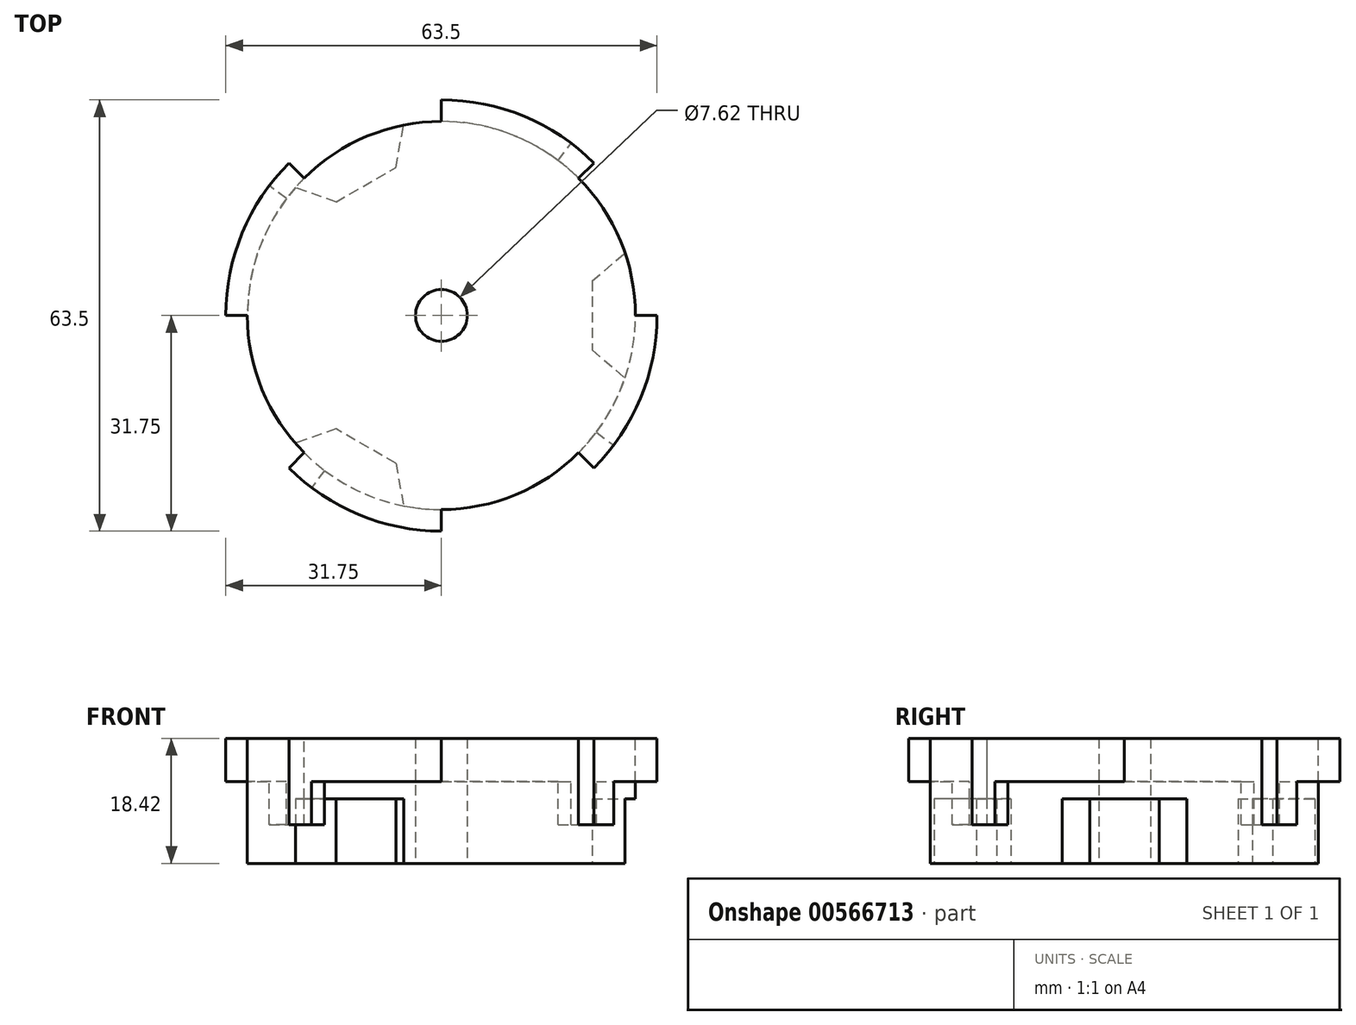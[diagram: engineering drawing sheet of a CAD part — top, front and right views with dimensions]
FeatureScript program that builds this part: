
annotation { "Feature Type Name" : "Feature", "Feature Type Description" : "" }
export const myFeature = defineFeature(function(context is Context, id is Id, definition is map)
    precondition{}
    {
        {
            var Q0;
            Q0=qCreatedBy(makeId("Top.planeOp"),FACE);
            var sketch = newSketch(context, id + "F0", { "sketchPlane" : qUnion([Q0])});
            skCircle(sketch, "E0", {"center": v(0, 0) * mm, "radius": 28.58 * mm});
            skLineSegment(sketch, "E1", {"start": v(22.23, 0) * mm, "end": v(22.23, 5.08) * mm});
            skLineSegment(sketch, "E2", {"start": v(22.23, 5.08) * mm, "end": v(27.05, 9.2) * mm});
            skLineSegment(sketch, "E3", {"start": v(22.23, 0) * mm, "end": v(22.23, -5.08) * mm});
            skLineSegment(sketch, "E4", {"start": v(22.23, -5.08) * mm, "end": v(27.05, -9.2) * mm});
            skLineSegment(sketch, "E5.1.0", {"start": v(-11.11, 19.25) * mm, "end": v(-15.51, 16.7) * mm});
            skLineSegment(sketch, "E5.1.1", {"start": v(-11.11, 19.25) * mm, "end": v(-6.71, 21.79) * mm});
            skLineSegment(sketch, "E5.1.2", {"start": v(-6.71, 21.79) * mm, "end": v(-5.55, 28.03) * mm});
            skLineSegment(sketch, "E5.1.3", {"start": v(-15.51, 16.7) * mm, "end": v(-21.5, 18.82) * mm});
            skLineSegment(sketch, "E5.2.0", {"start": v(-11.11, -19.25) * mm, "end": v(-6.71, -21.79) * mm});
            skLineSegment(sketch, "E5.2.1", {"start": v(-11.11, -19.25) * mm, "end": v(-15.51, -16.7) * mm});
            skLineSegment(sketch, "E5.2.2", {"start": v(-15.51, -16.7) * mm, "end": v(-21.5, -18.82) * mm});
            skLineSegment(sketch, "E5.2.3", {"start": v(-6.71, -21.79) * mm, "end": v(-5.55, -28.03) * mm});
            skCircle(sketch, "E6", {"center": v(0, 0) * mm, "radius": 3.81 * mm});
            skSolve(sketch);
        }
        {
            var Q0;
            Q0=makeQuery(id+"F0.imprint","IMPRINT",FACE,{"disambiguationData":[TD([[makeQuery(id+"F0.imprint","IMPRINT",EDGE,{"derivedFrom":sQuery(id+"F0.wireOp",EDGE,"E1")}),1.0]])]});
            extrude(context, id + "F1", {"entities" : qUnion([Q0]), "depth" : 9.52 * mm, "offsetDistance" : 25.4 * mm});
        }
        {
            var Q0;
            Q0=makeQuery(id+"F1.opExtrude","CAP_FACE",FACE,{"disambiguationData":[OSD([sQuery(id+"F0.wireOp",EDGE,"E0"),sQuery(id+"F0.wireOp",EDGE,"E1"),sQuery(id+"F0.wireOp",EDGE,"E2"),sQuery(id+"F0.wireOp",EDGE,"E3"),sQuery(id+"F0.wireOp",EDGE,"E4"),sQuery(id+"F0.wireOp",EDGE,"E5.1.0"),sQuery(id+"F0.wireOp",EDGE,"E5.1.1"),sQuery(id+"F0.wireOp",EDGE,"E5.1.2"),sQuery(id+"F0.wireOp",EDGE,"E5.1.3"),sQuery(id+"F0.wireOp",EDGE,"E5.2.0"),sQuery(id+"F0.wireOp",EDGE,"E5.2.1"),sQuery(id+"F0.wireOp",EDGE,"E5.2.2"),sQuery(id+"F0.wireOp",EDGE,"E5.2.3"),sQuery(id+"F0.wireOp",EDGE,"E6")])],"isStart":false});
            var sketch = newSketch(context, id + "F2", { "sketchPlane" : qUnion([Q0])});
            skCircle(sketch, "E7", {"center": v(0, 0) * mm, "radius": 28.58 * mm});
            skLineSegment(sketch, "E8", {"start": v(-21.5, 18.82) * mm, "end": v(-18.24, 17.67) * mm});
            skLineSegment(sketch, "E9", {"start": v(-5.55, 28.03) * mm, "end": v(-6.18, 24.64) * mm});
            skLineSegment(sketch, "E10", {"start": v(27.05, 9.2) * mm, "end": v(24.43, 6.96) * mm});
            skLineSegment(sketch, "E11", {"start": v(27.05, -9.2) * mm, "end": v(24.43, -6.96) * mm});
            skLineSegment(sketch, "E12", {"start": v(-21.5, -18.82) * mm, "end": v(-18.24, -17.67) * mm});
            skLineSegment(sketch, "E13", {"start": v(-5.55, -28.03) * mm, "end": v(-6.18, -24.64) * mm});
            skCircle(sketch, "E14", {"center": v(0, 0) * mm, "radius": 3.81 * mm});
            skSolve(sketch);
        }
        {
            var Q0;
            Q0 = qSketchRegion(id + "F2", true);
            var Q1;
            Q1 = qSketchRegion(id + "F4", true);
            extrude(context, id + "F3", {"entities" : qUnion([Q0, Q1]), "operationType" : NewBodyOperationType.ADD, "depth" : 8.9 * mm, "offsetDistance" : 25.4 * mm});
        }
        {
            var Q0;
            Q0=qCreatedBy(makeId("Right.planeOp"),FACE);
            var sketch = newSketch(context, id + "F4", { "sketchPlane" : qUnion([Q0])});
            skLineSegment(sketch, "E15", {"start": v(0, 0) * mm, "end": v(-28.58, 0) * mm});
            skLineSegment(sketch, "E16", {"start": v(-28.58, 0) * mm, "end": v(-28.58, 18.41) * mm});
            skLineSegment(sketch, "E17", {"start": v(-28.58, 18.41) * mm, "end": v(-31.75, 18.41) * mm});
            skLineSegment(sketch, "E18", {"start": v(-31.75, 18.41) * mm, "end": v(-31.75, 12.06) * mm});
            skLineSegment(sketch, "E19", {"start": v(-31.75, 12.06) * mm, "end": v(-28.58, 12.06) * mm});
            skLineSegment(sketch, "E20", {"start": v(0, 0) * mm, "end": v(0, 23.45) * mm});
            skSolve(sketch);
        }
        {
            var Q0;
            Q0 = qSketchRegion(id + "F4", true);
            var Q1;
            Q1=sQuery(id+"F4.wireOp",EDGE,"E20");
            revolve(context, id + "F5", {"operationType" : NewBodyOperationType.ADD, "entities" : qUnion([Q0]), "axis" : qUnion([Q1]), "revolveType" : RevolveType.FULL});
        }
        {
            var Q0;
            Q0=makeQuery(id+"F5.boolean.opBoolean","MERGE",FACE,{"derivedFrom":[makeQuery(id+"F3.opExtrude","CAP_FACE",FACE,{"disambiguationData":[OSD([sQuery(id+"F2.wireOp",EDGE,"E7"),sQuery(id+"F2.wireOp",EDGE,"E14")])],"isStart":false}),makeQuery(id+"F5.opRevolve","SWEPT_FACE",FACE,{"disambiguationData":[OSD([sQuery(id+"F4.wireOp",EDGE,"E17")])]})]});
            var sketch = newSketch(context, id + "F6", { "sketchPlane" : qUnion([Q0])});
            skArc(sketch, "E21", {"start": v(28.58, 0) * mm, "mid": v(26.4, 10.94) * mm, "end": v(20.2, 20.2) * mm});
            skArc(sketch, "E22", {"start": v(31.75, 0) * mm, "mid": v(29.33, 12.15) * mm, "end": v(22.45, 22.45) * mm});
            skLineSegment(sketch, "E23", {"start": v(28.58, 0) * mm, "end": v(31.75, 0) * mm});
            skLineSegment(sketch, "E24", {"start": v(0, 28.58) * mm, "end": v(0, 31.75) * mm});
            skLineSegment(sketch, "E25", {"start": v(0, -28.58) * mm, "end": v(0, -31.75) * mm});
            skLineSegment(sketch, "E26", {"start": v(-28.58, 0) * mm, "end": v(-31.75, 0) * mm});
            skLineSegment(sketch, "E27", {"start": v(20.2, -20.2) * mm, "end": v(22.45, -22.45) * mm});
            skLineSegment(sketch, "E28", {"start": v(20.2, 20.2) * mm, "end": v(22.45, 22.45) * mm});
            skLineSegment(sketch, "E29", {"start": v(-20.2, -20.2) * mm, "end": v(-22.45, -22.45) * mm});
            skLineSegment(sketch, "E30", {"start": v(-20.2, 20.2) * mm, "end": v(-22.45, 22.45) * mm});
            skArc(sketch, "E31.trimOffspring", {"start": v(0, -28.58) * mm, "mid": v(10.94, -26.4) * mm, "end": v(20.2, -20.2) * mm});
            skArc(sketch, "E32.trimOffspring", {"start": v(0, -31.75) * mm, "mid": v(12.15, -29.33) * mm, "end": v(22.45, -22.45) * mm});
            skArc(sketch, "E33.trimOffspring", {"start": v(-28.58, 0) * mm, "mid": v(-26.4, -10.94) * mm, "end": v(-20.2, -20.2) * mm});
            skArc(sketch, "E34.trimOffspring", {"start": v(-31.75, 0) * mm, "mid": v(-29.33, -12.15) * mm, "end": v(-22.45, -22.45) * mm});
            skArc(sketch, "E35.trimOffspring", {"start": v(0, 28.58) * mm, "mid": v(-10.94, 26.4) * mm, "end": v(-20.2, 20.2) * mm});
            skArc(sketch, "E36.trimOffspring", {"start": v(0, 31.75) * mm, "mid": v(-12.15, 29.33) * mm, "end": v(-22.45, 22.45) * mm});
            skSolve(sketch);
        }
        {
            var Q0;
            Q0 = qSketchRegion(id + "F6", true);
            extrude(context, id + "F7", {"entities" : qUnion([Q0]), "operationType" : NewBodyOperationType.REMOVE, "oppositeDirection" : true, "depth" : 6.35 * mm, "offsetDistance" : 25.4 * mm});
        }
        {
            var Q0;
            Q0=makeQuery(id+"F7.boolean.opBoolean","SPLIT",FACE,{"disambiguationData":[TD([makeQuery(id+"F7.opExtrude","SWEPT_FACE",FACE,{"disambiguationData":[OSD([sQuery(id+"F6.wireOp",EDGE,"E23")])]})])],"derivedFrom":makeQuery(id+"F5.opRevolve","SWEPT_FACE",FACE,{"disambiguationData":[OSD([sQuery(id+"F4.wireOp",EDGE,"E19")])]})});
            var sketch = newSketch(context, id + "F8", { "sketchPlane" : qUnion([Q0])});
            skCircle(sketch, "E37", {"center": v(0, 0) * mm, "radius": 31.75 * mm});
            skCircle(sketch, "E38", {"center": v(0, 0) * mm, "radius": 28.58 * mm});
            skLineSegment(sketch, "E39", {"start": v(20.2, 20.2) * mm, "end": v(22.45, 22.45) * mm});
            skLineSegment(sketch, "E40", {"start": v(0, 0) * mm, "end": v(25.36, 19.1) * mm});
            skLineSegment(sketch, "E41.1.0", {"start": v(20.2, -20.2) * mm, "end": v(22.45, -22.45) * mm});
            skLineSegment(sketch, "E41.1.2", {"start": v(0, 0) * mm, "end": v(19.1, -25.36) * mm});
            skLineSegment(sketch, "E41.2.0", {"start": v(-20.2, -20.2) * mm, "end": v(-22.45, -22.45) * mm});
            skLineSegment(sketch, "E41.2.2", {"start": v(0, 0) * mm, "end": v(-25.36, -19.1) * mm});
            skLineSegment(sketch, "E41.3.0", {"start": v(-20.2, 20.2) * mm, "end": v(-22.45, 22.45) * mm});
            skLineSegment(sketch, "E41.3.2", {"start": v(0, 0) * mm, "end": v(-19.1, 25.36) * mm});
            skLineSegment(sketch, "E41.anchor1", {"start": v(0, 0) * mm, "end": v(20.2, 20.2) * mm, "construction": true});
            skLineSegment(sketch, "E41.anchor2", {"start": v(0, 0) * mm, "end": v(-20.2, 20.2) * mm, "construction": true});
            skSolve(sketch);
        }
        {
            var Q0;
            {var subQ0=sQuery(id+"F8.wireOp",EDGE,"E39");Q0=makeQuery(id+"F8.imprint","IMPRINT",FACE,{"disambiguationData":[TD([[makeQuery(id+"F8.imprint","IMPRINT",EDGE,{"derivedFrom":subQ0}),-1.0]])]});}
            var Q1;
            {var subQ0=sQuery(id+"F8.wireOp",EDGE,"E41.1.0");Q1=makeQuery(id+"F8.imprint","IMPRINT",FACE,{"disambiguationData":[TD([[makeQuery(id+"F8.imprint","IMPRINT",EDGE,{"derivedFrom":subQ0}),-1.0]])]});}
            var Q2;
            {var subQ0=sQuery(id+"F8.wireOp",EDGE,"E41.2.0");Q2=makeQuery(id+"F8.imprint","IMPRINT",FACE,{"disambiguationData":[TD([[makeQuery(id+"F8.imprint","IMPRINT",EDGE,{"derivedFrom":subQ0}),-1.0]])]});}
            var Q3;
            {var subQ0=sQuery(id+"F8.wireOp",EDGE,"E41.3.0");Q3=makeQuery(id+"F8.imprint","IMPRINT",FACE,{"disambiguationData":[TD([[makeQuery(id+"F8.imprint","IMPRINT",EDGE,{"derivedFrom":subQ0}),-1.0]])]});}
            extrude(context, id + "F9", {"entities" : qUnion([Q0, Q1, Q2, Q3]), "operationType" : NewBodyOperationType.ADD, "depth" : 6.35 * mm, "offsetDistance" : 25.4 * mm});
        }
    });
